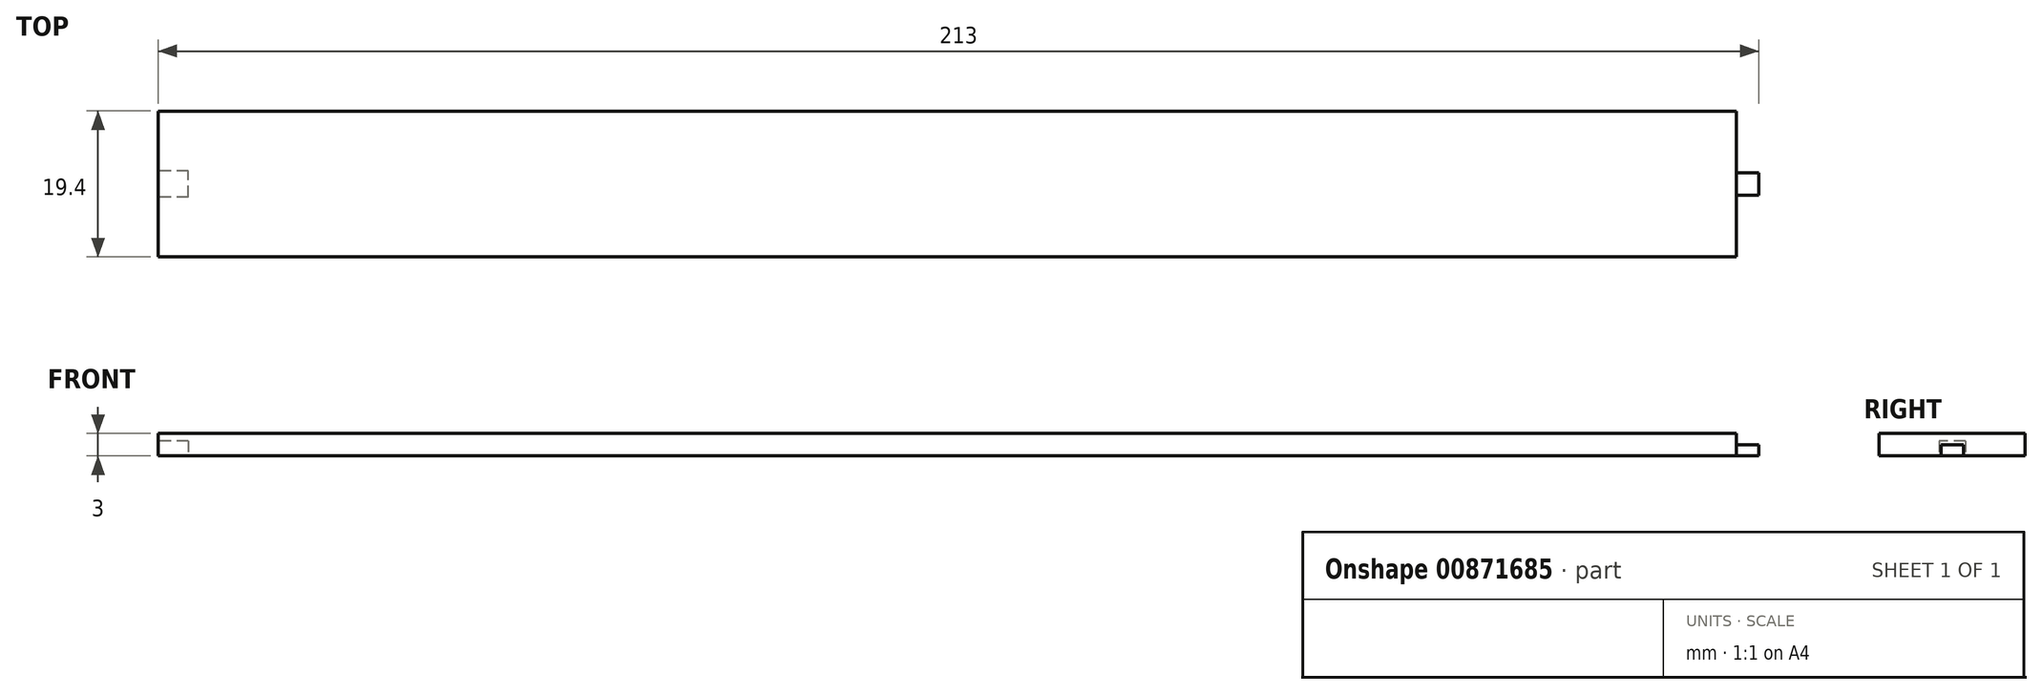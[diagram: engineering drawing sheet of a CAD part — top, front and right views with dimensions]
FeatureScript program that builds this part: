
annotation { "Feature Type Name" : "Feature", "Feature Type Description" : "" }
export const myFeature = defineFeature(function(context is Context, id is Id, definition is map)
    precondition{}
    {
        {
            var Q0;
            Q0=qCreatedBy(makeId("Top.planeOp"),FACE);
            var sketch = newSketch(context, id + "F0", { "sketchPlane" : qUnion([Q0])});
            skLineSegment(sketch, "E0.bottom", {"start": v(105, -9.7) * mm, "end": v(-105, -9.7) * mm});
            skLineSegment(sketch, "E0.top", {"start": v(105, 9.7) * mm, "end": v(-105, 9.7) * mm});
            skLineSegment(sketch, "E0.left", {"start": v(105, -9.7) * mm, "end": v(105, 9.7) * mm});
            skLineSegment(sketch, "E0.right", {"start": v(-105, -9.7) * mm, "end": v(-105, 9.7) * mm});
            skPoint(sketch, "E0.middle", {"position": v(0, 0) * mm});
            skSolve(sketch);
        }
        {
            var Q0;
            Q0=qSketchRegion(id+"F0",true);
            extrude(context, id + "F1", {"entities" : qUnion([Q0]), "depth" : 3 * mm, "offsetDistance" : 25 * mm});
        }
        {
            var Q0;
            Q0=makeQuery(id+"F1.opExtrude","SWEPT_FACE",FACE,{"disambiguationData":[OSD([sQuery(id+"F0.wireOp",EDGE,"E0.left")])]});
            var sketch = newSketch(context, id + "F2", { "sketchPlane" : qUnion([Q0])});
            skLineSegment(sketch, "E1.bottom", {"start": v(-1.5, 1.5) * mm, "end": v(1.5, 1.5) * mm});
            skLineSegment(sketch, "E1.top", {"start": v(-1.5, 0) * mm, "end": v(1.5, 0) * mm});
            skLineSegment(sketch, "E1.left", {"start": v(-1.5, 1.5) * mm, "end": v(-1.5, 0) * mm});
            skLineSegment(sketch, "E1.right", {"start": v(1.5, 1.5) * mm, "end": v(1.5, 0) * mm});
            skLineSegment(sketch, "E2", {"start": v(0, 0) * mm, "end": v(0, 1.96) * mm, "construction": true});
            skSolve(sketch);
        }
        {
            var Q0;
            Q0=qSketchRegion(id+"F2",true);
            extrude(context, id + "F3", {"entities" : qUnion([Q0]), "operationType" : NewBodyOperationType.ADD, "depth" : 3 * mm, "offsetDistance" : 25 * mm});
        }
        {
            var Q0;
            Q0=makeQuery(id+"F1.opExtrude","SWEPT_FACE",FACE,{"disambiguationData":[OSD([sQuery(id+"F0.wireOp",EDGE,"E0.right")])]});
            var sketch = newSketch(context, id + "F4", { "sketchPlane" : qUnion([Q0])});
            skLineSegment(sketch, "E3.bottom", {"start": v(-1.75, 2) * mm, "end": v(1.75, 2) * mm});
            skLineSegment(sketch, "E3.top", {"start": v(-1.75, 0) * mm, "end": v(1.75, 0) * mm});
            skLineSegment(sketch, "E3.left", {"start": v(-1.75, 2) * mm, "end": v(-1.75, 0) * mm});
            skLineSegment(sketch, "E3.right", {"start": v(1.75, 2) * mm, "end": v(1.75, 0) * mm});
            skLineSegment(sketch, "E4", {"start": v(0, 0) * mm, "end": v(0, 3) * mm, "construction": true});
            skSolve(sketch);
        }
        {
            var Q0;
            Q0 = qSketchRegion(id + "F4", true);
            extrude(context, id + "F5", {"entities" : qUnion([Q0]), "operationType" : NewBodyOperationType.REMOVE, "oppositeDirection" : true, "depth" : 4 * mm, "offsetDistance" : 25 * mm});
        }
    });
